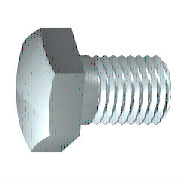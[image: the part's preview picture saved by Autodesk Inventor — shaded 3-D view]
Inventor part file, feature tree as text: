
AUTODESK INVENTOR PART (.ipt)
format: ipt  version: 2020 (Build 240168000, 168)  size: 193,536 bytes
history: native  units: mm (DEFAULTED — no unit token found)
features: sketch x3, extrude x1, chamfer x1, plane x1
ambient origin geometry x7: Origin, YZ Plane, XZ Plane, X Axis, Y Axis, Z Axis, Center Point
bodies: Solid1 (feature_tree), Body (feature_tree)
feature tree (6):
  extrude  "Head"  Depth=47.9mm
  chamfer  "Chamfer1"  Distance=2.4mm
  plane  "Work Plane1"
  sketch  "Sketch1"  dims[d0=50.0mm d1=47.9mm]
  sketch  "Sketch2"  dims[d2=4.0mm]
  sketch  "Sketch4"  dims[d12=90.0deg d3=2.4mm d4=0.0mm d5=30.0deg d21=90.0deg d6=0.429415mm d7=0.429515mm d8=0.0mm d9=0.4001mm d10=5.9mm d11=7.0mm d13=0.429515mm d14=3.621114mm d15=47.9mm d16=0.0mm d19=7.0mm d55=45.0deg d57=0.0mm d58=0.0mm]
